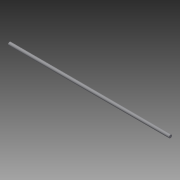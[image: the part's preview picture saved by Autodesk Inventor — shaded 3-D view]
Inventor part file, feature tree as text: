
AUTODESK INVENTOR PART (.ipt)
format: ipt  version: 2015 (Build 190159000, 159)  size: 70,144 bytes
history: native  units: in
note: dims shown in document units (in); Inventor stores cm internally (conversion verified against a paired STEP export)
features: extrude x1, sketch x1
ambient origin geometry x8: Origin, YZ Plane, XZ Plane, XY Plane, X Axis, Y Axis, Z Axis, Center Point
bodies: Solid1 (feature_tree)
feature tree (2):
  extrude  "Extrusion1"  Depth=13.0in TaperAngle=0.0deg
  sketch  "Sketch1"  dims[d0=0.25in d1=13.0in d2=0.0in]
